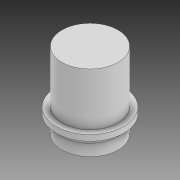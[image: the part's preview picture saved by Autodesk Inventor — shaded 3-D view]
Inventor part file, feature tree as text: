
AUTODESK INVENTOR PART (.ipt)
format: ipt  version: 2020 (Build 240168000, 168)  size: 98,304 bytes
history: native  units: mm
features: revolve x1, sketch x1
ambient origin geometry x8: Origin, YZ Plane, XZ Plane, XY Plane, X Axis, Y Axis, Z Axis, Center Point
bodies: Solid1 (feature_tree)
feature tree (2):
  revolve  "Revolution1"  [1 undecoded]
  sketch  "Sketch1"  dims[d0=2.4mm d1=1.0mm d2=1.0mm d3=4.5mm d7=45.0deg d8=0.5mm d9=90.0deg]
note: 1 required parameter value undecoded (feature->parameter linkage not recoverable at this tier; creation-order binding heuristic only, values carry confidence <= 0.55)
